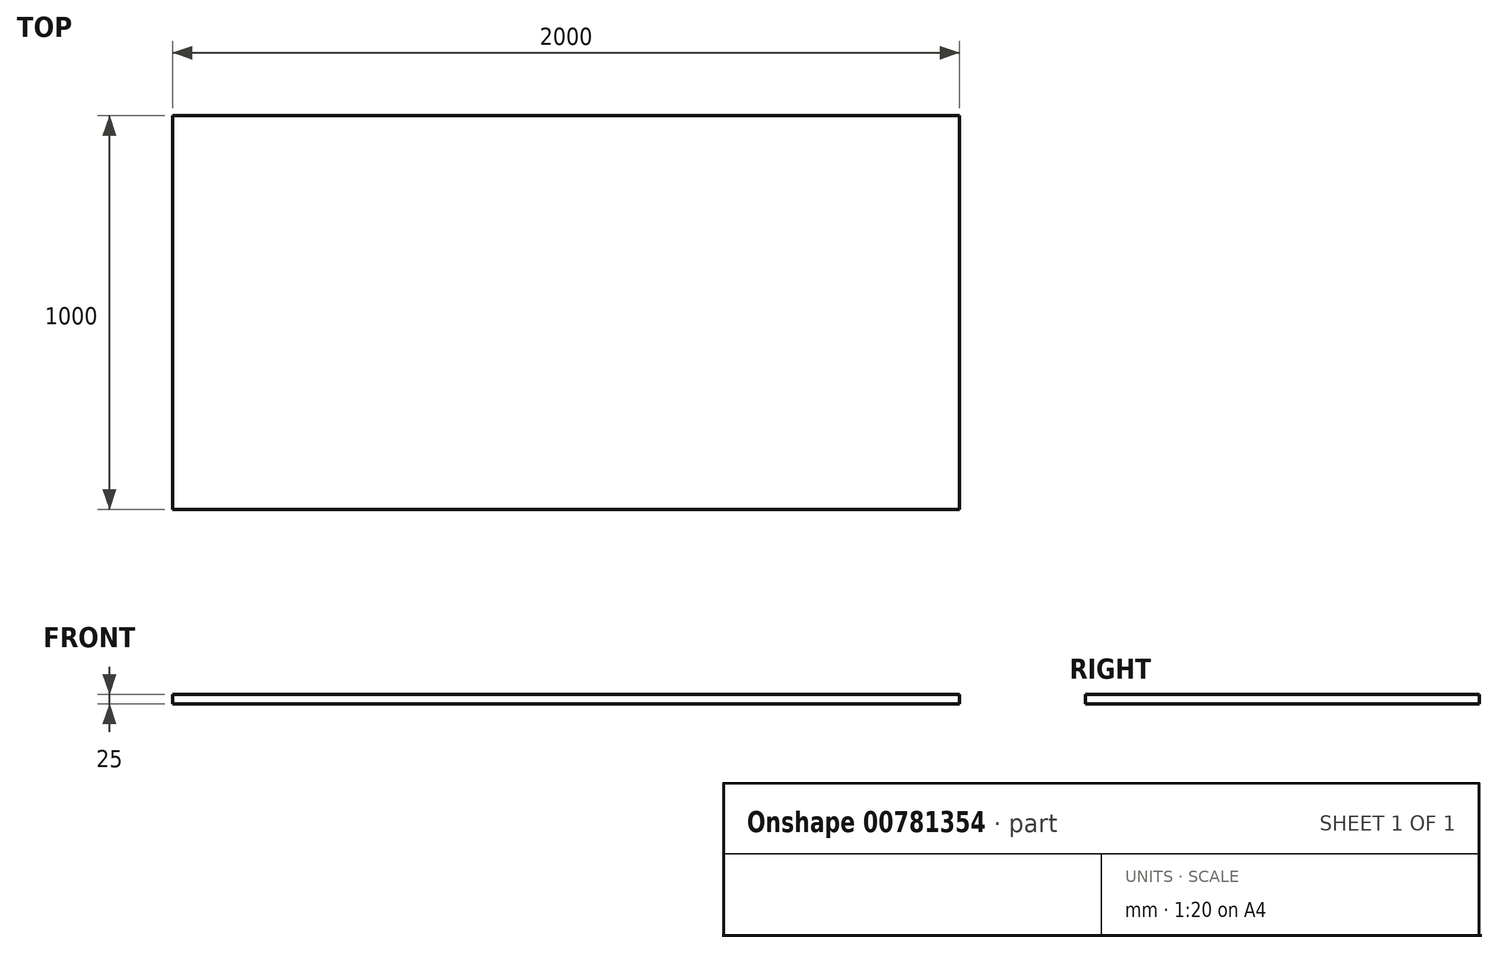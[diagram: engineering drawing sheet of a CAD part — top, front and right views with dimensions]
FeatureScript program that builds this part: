
annotation { "Feature Type Name" : "Feature", "Feature Type Description" : "" }
export const myFeature = defineFeature(function(context is Context, id is Id, definition is map)
    precondition{}
    {
        {
            var Q0;
            Q0=qCreatedBy(makeId("Top.planeOp"),FACE);
            var sketch = newSketch(context, id + "F0", { "sketchPlane" : qUnion([Q0])});
            skLineSegment(sketch, "E0.bottom", {"start": v(0, 0) * mm, "end": v(2000, 0) * mm});
            skLineSegment(sketch, "E0.top", {"start": v(0, 1000) * mm, "end": v(2000, 1000) * mm});
            skLineSegment(sketch, "E0.left", {"start": v(0, 0) * mm, "end": v(0, 1000) * mm});
            skLineSegment(sketch, "E0.right", {"start": v(2000, 0) * mm, "end": v(2000, 1000) * mm});
            skSolve(sketch);
        }
        {
            var Q0;
            Q0=makeQuery(id+"F0.imprint","IMPRINT",FACE,{"disambiguationData":[TD([[makeQuery(id+"F0.imprint","IMPRINT",EDGE,{"derivedFrom":sQuery(id+"F0.wireOp",EDGE,"E0.bottom")}),1.0]])]});
            extrude(context, id + "F1", {"entities" : qUnion([Q0]), "depth" : 25 * mm, "offsetDistance" : 25 * mm});
        }
    });
